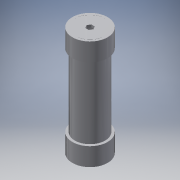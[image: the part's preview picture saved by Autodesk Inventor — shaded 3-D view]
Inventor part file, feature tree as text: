
AUTODESK INVENTOR PART (.ipt)
format: ipt  version: 2016 (Build 200138000, 138)  size: 145,408 bytes
history: native  units: in
note: dims shown in document units (in); Inventor stores cm internally (conversion verified against a paired STEP export)
features: extrude x6, sketch x6
ambient origin geometry x8: Origin, YZ Plane, XZ Plane, XY Plane, X Axis, Y Axis, Z Axis, Center Point
bodies: Body1 (feature_tree)
feature tree (12):
  extrude  "Extrusion5"  Depth=0.203in
  extrude  "Extrusion6"  Depth=7.5in
  extrude  "Extrusion7"  Depth=1.5in TaperAngle=0.0deg
  extrude  "Extrusion8"  Depth=1.5in TaperAngle=0.0deg
  extrude  "Extrusion9"  Depth=0.203in TaperAngle=0.0deg
  extrude  "Extrusion10"  Depth=9.0in TaperAngle=0.0deg
  sketch  "Sketch6"  dims[d16=2.5in d17=0.203in]
  sketch  "Sketch7"  dims[d18=7.5in d19=0.0in d20=2.5in]
  sketch  "Sketch8"  dims[d21=0.203in d22=1.5in d23=0.0in]
  sketch  "Sketch9"  dims[d24=0.203in d25=0.0in d26=1.5in d27=0.0in]
  sketch  "Sketch10"  dims[d28=2.4996in d29=0.203in d30=0.0in]
  sketch  "Sketch11"  dims[d31=0.5in d32=9.0in d33=0.0in]
